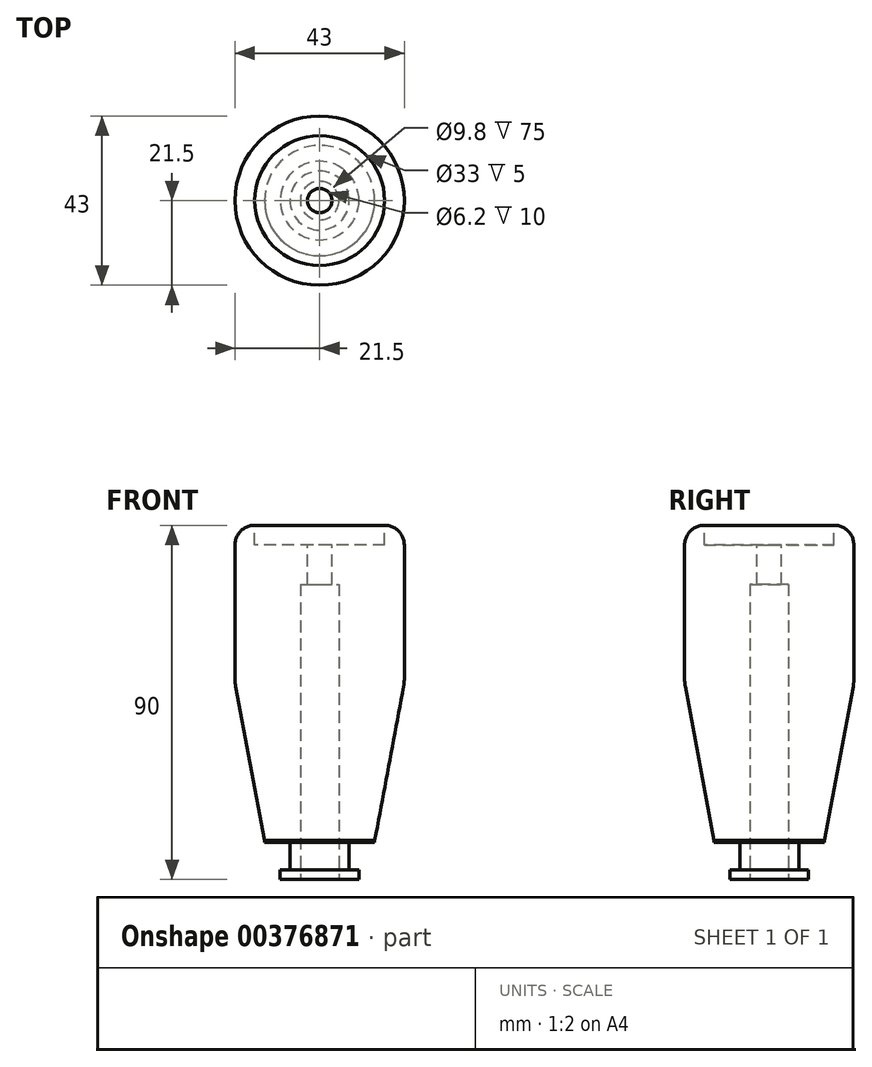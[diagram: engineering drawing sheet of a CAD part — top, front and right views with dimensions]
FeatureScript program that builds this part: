
annotation { "Feature Type Name" : "Feature", "Feature Type Description" : "" }
export const myFeature = defineFeature(function(context is Context, id is Id, definition is map)
    precondition{}
    {
        {
            var Q0;
            Q0=qCreatedBy(makeId("Top.planeOp"),FACE);
            var sketch = newSketch(context, id + "F0", { "sketchPlane" : qUnion([Q0])});
            skCircle(sketch, "E0", {"center": v(0, 0) * mm, "radius": 21.5 * mm});
            skSolve(sketch);
        }
        {
            var Q0;
            Q0=makeQuery(id+"F0.imprint","IMPRINT",FACE,{"disambiguationData":[TD([[makeQuery(id+"F0.imprint","IMPRINT",EDGE,{"derivedFrom":sQuery(id+"F0.wireOp",EDGE,"E0")}),1.0]])]});
            extrude(context, id + "F1", {"entities" : qUnion([Q0]), "depth" : 40 * mm});
        }
        {
            var Q0;
            Q0=makeQuery(id+"F1.opExtrude","CAP_EDGE",EDGE,{"disambiguationData":[OSD([sQuery(id+"F0.wireOp",EDGE,"E0")])],"isStart":false});
            fillet(context, id + "F2", {"entities" : qUnion([Q0]), "radius" : 5 * mm, "tangentPropagation" : true, "allowEdgeOverflow" : false});
        }
        {
            var Q0;
            Q0=makeQuery(id+"F1.opExtrude","CAP_FACE",FACE,{"disambiguationData":[OSD([sQuery(id+"F0.wireOp",EDGE,"E0")])],"isStart":true});
            var sketch = newSketch(context, id + "F3", { "sketchPlane" : qUnion([Q0])});
            skCircle(sketch, "E1", {"center": v(0, 0) * mm, "radius": 21.5 * mm});
            skSolve(sketch);
        }
        {
            var Q0;
            Q0=makeQuery(id+"F3.imprint","IMPRINT",FACE,{"disambiguationData":[TD([[makeQuery(id+"F3.imprint","IMPRINT",EDGE,{"derivedFrom":sQuery(id+"F3.wireOp",EDGE,"E1")}),-1.0]])]});
            extrude(context, id + "F4", {"entities" : qUnion([Q0]), "operationType" : NewBodyOperationType.ADD, "depth" : 40 * mm});
        }
        {
            var Q0;
            Q0=makeQuery(id+"F4.opExtrude","CAP_EDGE",EDGE,{"disambiguationData":[OSD([sQuery(id+"F3.wireOp",EDGE,"E1")])],"isStart":false});
            chamfer(context, id + "F5", {"entities" : qUnion([Q0]), "chamferType" : ChamferType.TWO_OFFSETS, "width1" : 40 * mm, "oppositeDirection" : false, "width2" : 7.5 * mm, "tangentPropagation" : true});
        }
        {
            var Q0;
            Q0=makeQuery(id+"F4.opExtrude","CAP_FACE",FACE,{"disambiguationData":[OSD([sQuery(id+"F3.wireOp",EDGE,"E1")])],"isStart":false});
            extrude(context, id + "F6", {"entities" : qUnion([Q0]), "operationType" : NewBodyOperationType.ADD, "depth" : 10 * mm});
        }
        {
            var Q0;
            {var subQ0=sQuery(id+"F3.wireOp",EDGE,"E1");Q0=makeQuery(id+"F5.opChamfer","BLEND_EDGE",EDGE,{"blendedFrom":[makeQuery(id+"F4.opExtrude","CAP_EDGE",EDGE,{"disambiguationData":[OSD([subQ0])],"isStart":false}),makeQuery(id+"F4.boolean.opBoolean","MERGE",FACE,{"derivedFrom":[makeQuery(id+"F1.opExtrude","SWEPT_FACE",FACE,{"disambiguationData":[OSD([sQuery(id+"F0.wireOp",EDGE,"E0")])]}),makeQuery(id+"F4.opExtrude","SWEPT_FACE",FACE,{"disambiguationData":[OSD([subQ0])]})]})],"blendedInto":[makeQuery(id+"F4.boolean.opBoolean","MERGE",FACE,{"derivedFrom":[makeQuery(id+"F1.opExtrude","SWEPT_FACE",FACE,{"disambiguationData":[OSD([sQuery(id+"F0.wireOp",EDGE,"E0")])]}),makeQuery(id+"F4.opExtrude","SWEPT_FACE",FACE,{"disambiguationData":[OSD([subQ0])]})]})]});}
            fillet(context, id + "F7", {"entities" : qUnion([Q0]), "radius" : 10 * mm, "tangentPropagation" : true, "allowEdgeOverflow" : false});
        }
        {
            var Q0;
            Q0=qCreatedBy(makeId("Right.planeOp"),FACE);
            var sketch = newSketch(context, id + "F8", { "sketchPlane" : qUnion([Q0])});
            skLineSegment(sketch, "E2.bottom", {"start": v(-17.43, -40.5) * mm, "end": v(-7.5, -40.5) * mm});
            skLineSegment(sketch, "E2.top", {"start": v(-10, -47.5) * mm, "end": v(-7.5, -47.5) * mm});
            skLineSegment(sketch, "E2.left", {"start": v(-17.43, -40.5) * mm, "end": v(-17.43, -47.5) * mm});
            skLineSegment(sketch, "E2.right", {"start": v(-7.5, -40.5) * mm, "end": v(-7.5, -47.5) * mm});
            skLineSegment(sketch, "E3", {"start": v(0, -39.98) * mm, "end": v(0, -66.82) * mm, "construction": true});
            skPoint(sketch, "E4.oppositeSnap0", {"position": v(-17.43, -44) * mm});
            skLineSegment(sketch, "E4.top", {"start": v(-10, -53.66) * mm, "end": v(-17.43, -53.66) * mm});
            skLineSegment(sketch, "E4.left", {"start": v(-10, -47.5) * mm, "end": v(-10, -53.66) * mm});
            skLineSegment(sketch, "E4.right", {"start": v(-17.43, -47.5) * mm, "end": v(-17.43, -53.66) * mm});
            skSolve(sketch);
        }
        {
            var Q0;
            Q0=makeQuery(id+"F8.imprint","IMPRINT",FACE,{"disambiguationData":[TD([[makeQuery(id+"F8.imprint","IMPRINT",EDGE,{"derivedFrom":sQuery(id+"F8.wireOp",EDGE,"E2.bottom")}),-1.0]])]});
            var Q1;
            Q1=sQuery(id+"F8.wireOp",EDGE,"E3");
            revolve(context, id + "F9", {"operationType" : NewBodyOperationType.REMOVE, "entities" : qUnion([Q0]), "axis" : qUnion([Q1]), "revolveType" : RevolveType.FULL, "oppositeDirection" : true});
        }
        {
            var Q0;
            Q0=makeQuery(id+"F6.opExtrude","CAP_FACE",FACE,{"disambiguationData":[OSD([sQuery(id+"F3.wireOp",EDGE,"E1")])],"isStart":false});
            var sketch = newSketch(context, id + "F10", { "sketchPlane" : qUnion([Q0])});
            skCircle(sketch, "E5", {"center": v(0, 0) * mm, "radius": 4.9 * mm});
            skSolve(sketch);
        }
        {
            var Q0;
            Q0=makeQuery(id+"F10.imprint","IMPRINT",FACE,{"disambiguationData":[TD([[makeQuery(id+"F10.imprint","IMPRINT",EDGE,{"derivedFrom":sQuery(id+"F10.wireOp",EDGE,"E5")}),1.0]])]});
            extrude(context, id + "F11", {"entities" : qUnion([Q0]), "operationType" : NewBodyOperationType.REMOVE, "oppositeDirection" : true, "depth" : 75 * mm});
        }
        {
            var Q0;
            Q0=makeQuery(id+"F1.opExtrude","CAP_FACE",FACE,{"disambiguationData":[OSD([sQuery(id+"F0.wireOp",EDGE,"E0")])],"isStart":false});
            var sketch = newSketch(context, id + "F12", { "sketchPlane" : qUnion([Q0])});
            skCircle(sketch, "E6", {"center": v(0, 0) * mm, "radius": 16.5 * mm});
            skSolve(sketch);
        }
        {
            var Q0;
            Q0=makeQuery(id+"F12.imprint","IMPRINT",FACE,{"disambiguationData":[TD([[makeQuery(id+"F12.imprint","IMPRINT",EDGE,{"derivedFrom":sQuery(id+"F12.wireOp",EDGE,"E6")}),1.0]])]});
            extrude(context, id + "F13", {"entities" : qUnion([Q0]), "operationType" : NewBodyOperationType.REMOVE, "oppositeDirection" : true, "depth" : 5 * mm});
        }
        {
            var Q0;
            Q0=makeQuery(id+"F13.boolean.opBoolean","COPY",FACE,{"derivedFrom":makeQuery(id+"F13.opExtrude","CAP_FACE",FACE,{"disambiguationData":[OSD([sQuery(id+"F12.wireOp",EDGE,"E6")])],"isStart":false})});
            var sketch = newSketch(context, id + "F14", { "sketchPlane" : qUnion([Q0])});
            skCircle(sketch, "E7", {"center": v(0, 0) * mm, "radius": 3.1 * mm});
            skSolve(sketch);
        }
        {
            var Q0;
            Q0=makeQuery(id+"F14.imprint","IMPRINT",FACE,{"disambiguationData":[TD([[makeQuery(id+"F14.imprint","IMPRINT",EDGE,{"derivedFrom":sQuery(id+"F14.wireOp",EDGE,"E7")}),1.0]])]});
            extrude(context, id + "F15", {"entities" : qUnion([Q0]), "operationType" : NewBodyOperationType.REMOVE, "endBound" : BoundingType.THROUGH_ALL, "oppositeDirection" : true, "depth" : 25 * mm});
        }
    });
